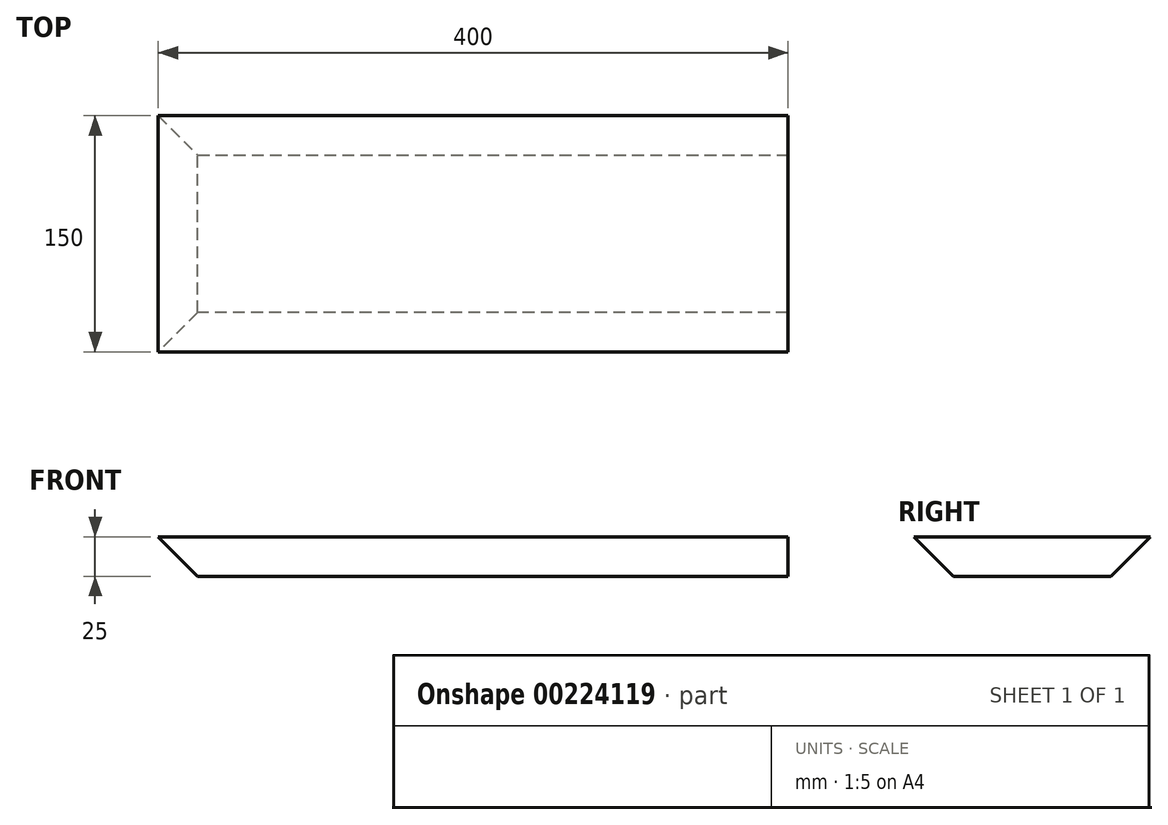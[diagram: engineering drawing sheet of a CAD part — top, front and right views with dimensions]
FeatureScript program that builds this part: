
annotation { "Feature Type Name" : "Feature", "Feature Type Description" : "" }
export const myFeature = defineFeature(function(context is Context, id is Id, definition is map)
    precondition{}
    {
        {
            var Q0;
            Q0=qCreatedBy(makeId("Top.planeOp"),FACE);
            var sketch = newSketch(context, id + "F0", { "sketchPlane" : qUnion([Q0])});
            skLineSegment(sketch, "E0.bottom", {"start": v(-200, 75) * mm, "end": v(200, 75) * mm});
            skLineSegment(sketch, "E0.top", {"start": v(-200, -75) * mm, "end": v(200, -75) * mm});
            skLineSegment(sketch, "E0.left", {"start": v(-200, 75) * mm, "end": v(-200, -75) * mm});
            skLineSegment(sketch, "E0.right", {"start": v(200, 75) * mm, "end": v(200, -75) * mm});
            skLineSegment(sketch, "E1", {"start": v(0, 75) * mm, "end": v(0, -75) * mm, "construction": true});
            skLineSegment(sketch, "E2", {"start": v(-200, 0) * mm, "end": v(200, 0) * mm, "construction": true});
            skSolve(sketch);
        }
        {
            var Q0;
            Q0=makeQuery(id+"F0.imprint","IMPRINT",FACE,{"disambiguationData":[TD([[makeQuery(id+"F0.imprint","IMPRINT",EDGE,{"derivedFrom":sQuery(id+"F0.wireOp",EDGE,"E0.bottom")}),-1.0]])]});
            extrude(context, id + "F1", {"entities" : qUnion([Q0]), "endBound" : BoundingType.SYMMETRIC, "depth" : 25 * mm});
        }
        {
            var Q0;
            Q0=makeQuery(id+"F1.opExtrude","CAP_EDGE",EDGE,{"disambiguationData":[OSD([sQuery(id+"F0.wireOp",EDGE,"E0.bottom")])],"isStart":true});
            var Q1;
            Q1=makeQuery(id+"F1.opExtrude","CAP_EDGE",EDGE,{"disambiguationData":[OSD([sQuery(id+"F0.wireOp",EDGE,"E0.left")])],"isStart":true});
            var Q2;
            Q2=makeQuery(id+"F1.opExtrude","CAP_EDGE",EDGE,{"disambiguationData":[OSD([sQuery(id+"F0.wireOp",EDGE,"E0.top")])],"isStart":true});
            chamfer(context, id + "F2", {"entities" : qUnion([Q0, Q1, Q2]), "width" : 25 * mm, "tangentPropagation" : true});
        }
    });
